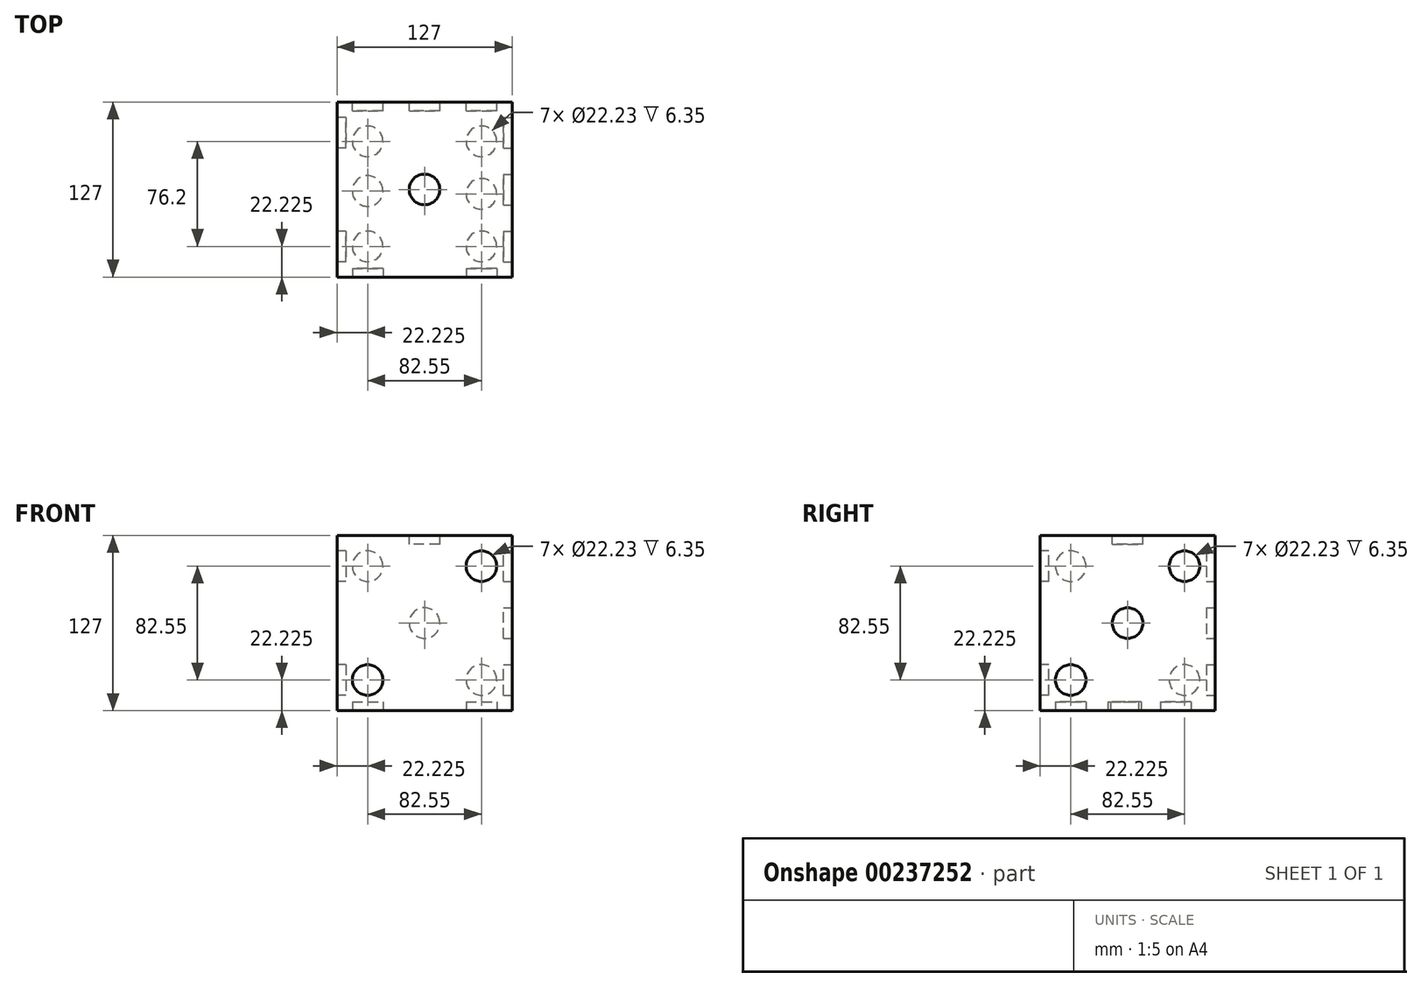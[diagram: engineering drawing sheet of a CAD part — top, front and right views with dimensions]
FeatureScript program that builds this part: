
annotation { "Feature Type Name" : "Feature", "Feature Type Description" : "" }
export const myFeature = defineFeature(function(context is Context, id is Id, definition is map)
    precondition{}
    {
        {
            var Q0;
            Q0=qCreatedBy(makeId("Top.planeOp"),FACE);
            var sketch = newSketch(context, id + "F0", { "sketchPlane" : qUnion([Q0])});
            skLineSegment(sketch, "E0.bottom", {"start": v(0, 0) * mm, "end": v(127, 0) * mm});
            skLineSegment(sketch, "E0.top", {"start": v(0, 127) * mm, "end": v(127, 127) * mm});
            skLineSegment(sketch, "E0.left", {"start": v(0, 0) * mm, "end": v(0, 127) * mm});
            skLineSegment(sketch, "E0.right", {"start": v(127, 0) * mm, "end": v(127, 127) * mm});
            skSolve(sketch);
        }
        {
            var Q0;
            Q0 = qSketchRegion(id + "F0", true);
            extrude(context, id + "F1", {"entities" : qUnion([Q0]), "depth" : 127 * mm});
        }
        {
            var Q0;
            Q0=makeQuery(id+"F1.opExtrude","CAP_FACE",FACE,{"disambiguationData":[OSD([sQuery(id+"F0.wireOp",EDGE,"E0.bottom"),sQuery(id+"F0.wireOp",EDGE,"E0.top"),sQuery(id+"F0.wireOp",EDGE,"E0.left"),sQuery(id+"F0.wireOp",EDGE,"E0.right")])],"isStart":false});
            var sketch = newSketch(context, id + "F2", { "sketchPlane" : qUnion([Q0])});
            skCircle(sketch, "E1", {"center": v(63.5, 63.5) * mm, "radius": 11.11 * mm});
            skSolve(sketch);
        }
        {
            var Q0;
            Q0 = qSketchRegion(id + "F2", true);
            extrude(context, id + "F3", {"entities" : qUnion([Q0]), "operationType" : NewBodyOperationType.REMOVE, "oppositeDirection" : true, "depth" : 6.35 * mm});
        }
        {
            var Q0;
            Q0=makeQuery(id+"F1.opExtrude","SWEPT_FACE",FACE,{"disambiguationData":[OSD([sQuery(id+"F0.wireOp",EDGE,"E0.bottom")])]});
            var sketch = newSketch(context, id + "F4", { "sketchPlane" : qUnion([Q0])});
            skCircle(sketch, "E2", {"center": v(22.23, 22.22) * mm, "radius": 11.11 * mm});
            skCircle(sketch, "E3", {"center": v(104.78, 104.78) * mm, "radius": 11.11 * mm});
            skSolve(sketch);
        }
        {
            var Q0;
            Q0 = qSketchRegion(id + "F4", true);
            extrude(context, id + "F5", {"entities" : qUnion([Q0]), "operationType" : NewBodyOperationType.REMOVE, "oppositeDirection" : true, "depth" : 6.35 * mm});
        }
        {
            var Q0;
            Q0=makeQuery(id+"F1.opExtrude","SWEPT_FACE",FACE,{"disambiguationData":[OSD([sQuery(id+"F0.wireOp",EDGE,"E0.right")])]});
            var sketch = newSketch(context, id + "F6", { "sketchPlane" : qUnion([Q0])});
            skLineSegment(sketch, "E4", {"start": v(0, 0) * mm, "end": v(127, 127) * mm, "construction": true});
            skCircle(sketch, "E5", {"center": v(22.22, 22.23) * mm, "radius": 11.11 * mm});
            skCircle(sketch, "E6", {"center": v(63.5, 63.5) * mm, "radius": 11.11 * mm});
            skCircle(sketch, "E7", {"center": v(104.77, 104.78) * mm, "radius": 11.11 * mm});
            skSolve(sketch);
        }
        {
            var Q0;
            Q0 = qSketchRegion(id + "F6", true);
            extrude(context, id + "F7", {"entities" : qUnion([Q0]), "operationType" : NewBodyOperationType.REMOVE, "oppositeDirection" : true, "depth" : 6.35 * mm});
        }
        {
            var Q0;
            Q0=makeQuery(id+"F1.opExtrude","SWEPT_FACE",FACE,{"disambiguationData":[OSD([sQuery(id+"F0.wireOp",EDGE,"E0.top")])]});
            var sketch = newSketch(context, id + "F8", { "sketchPlane" : qUnion([Q0])});
            skCircle(sketch, "E8", {"center": v(-63.5, 63.5) * mm, "radius": 11.11 * mm});
            skPoint(sketch, "E8.centerSnap0", {"position": v(-63.5, 127) * mm});
            skPoint(sketch, "E8.centerSnap1", {"position": v(-127, 63.5) * mm});
            skCircle(sketch, "E9", {"center": v(-104.77, 104.78) * mm, "radius": 11.11 * mm});
            skCircle(sketch, "E10", {"center": v(-22.23, 104.78) * mm, "radius": 11.11 * mm});
            skCircle(sketch, "E11", {"center": v(-104.77, 22.22) * mm, "radius": 11.11 * mm});
            skCircle(sketch, "E12", {"center": v(-22.23, 22.22) * mm, "radius": 11.11 * mm});
            skSolve(sketch);
        }
        {
            var Q0;
            Q0=makeQuery(id+"F1.opExtrude","SWEPT_FACE",FACE,{"disambiguationData":[OSD([sQuery(id+"F0.wireOp",EDGE,"E0.left")])]});
            var sketch = newSketch(context, id + "F9", { "sketchPlane" : qUnion([Q0])});
            skCircle(sketch, "E13", {"center": v(-104.78, 104.78) * mm, "radius": 11.11 * mm});
            skCircle(sketch, "E14", {"center": v(-22.23, 104.78) * mm, "radius": 11.11 * mm});
            skCircle(sketch, "E15", {"center": v(-104.78, 22.22) * mm, "radius": 11.11 * mm});
            skCircle(sketch, "E16", {"center": v(-22.23, 22.22) * mm, "radius": 11.11 * mm});
            skSolve(sketch);
        }
        {
            var Q0;
            Q0 = qSketchRegion(id + "F9", true);
            extrude(context, id + "F10", {"entities" : qUnion([Q0]), "operationType" : NewBodyOperationType.REMOVE, "oppositeDirection" : true, "depth" : 6.35 * mm});
        }
        {
            var Q0;
            Q0=makeQuery(id+"F1.opExtrude","CAP_FACE",FACE,{"disambiguationData":[OSD([sQuery(id+"F0.wireOp",EDGE,"E0.bottom"),sQuery(id+"F0.wireOp",EDGE,"E0.top"),sQuery(id+"F0.wireOp",EDGE,"E0.left"),sQuery(id+"F0.wireOp",EDGE,"E0.right")])],"isStart":true});
            var sketch = newSketch(context, id + "F11", { "sketchPlane" : qUnion([Q0])});
            skLineSegment(sketch, "E17", {"start": v(22.23, 0) * mm, "end": v(22.23, -120.65) * mm});
            skLineSegment(sketch, "E18", {"start": v(104.78, 0) * mm, "end": v(104.77, -120.65) * mm});
            skCircle(sketch, "E19", {"center": v(22.23, -22.23) * mm, "radius": 11.11 * mm});
            skCircle(sketch, "E20", {"center": v(22.23, -62.36) * mm, "radius": 11.11 * mm});
            skCircle(sketch, "E21", {"center": v(22.23, -98.43) * mm, "radius": 11.11 * mm});
            skCircle(sketch, "E22", {"center": v(104.77, -98.43) * mm, "radius": 11.11 * mm});
            skCircle(sketch, "E23", {"center": v(104.78, -60.33) * mm, "radius": 11.11 * mm});
            skCircle(sketch, "E24", {"center": v(104.77, -22.23) * mm, "radius": 11.11 * mm});
            skSolve(sketch);
        }
        {
            var Q0;
            Q0 = qSketchRegion(id + "F11", true);
            extrude(context, id + "F12", {"entities" : qUnion([Q0]), "operationType" : NewBodyOperationType.REMOVE, "oppositeDirection" : true, "depth" : 6.35 * mm});
        }
        {
            var Q0;
            Q0 = qSketchRegion(id + "F8", true);
            extrude(context, id + "F13", {"entities" : qUnion([Q0]), "operationType" : NewBodyOperationType.REMOVE, "oppositeDirection" : true, "depth" : 6.35 * mm});
        }
    });
